# Revit family: Mixer-Sink-Caroma Saracom
name_source: partatom
category: Plumbing Fixtures
revit_build: Autodesk Revit 2014 (Build: 20131024_2115(x64)
units: mm (PartAtom-declared; Revit-internal decimal feet)

## types (1)
- Standard
    Assembly Code = D2020300
    CW Connection = Yes
    CWFU = 1.98
    Connector Radius = 10 mm  [stored 0.0328084 ft]
    Cost = 0 $
    Default Elevation = 0 mm  [stored 0 ft]
    Description = The Saracom range offers the home owner the practical choice in using one stylish mixer design for the entire home, from the kitchen to the laundry to the bathroom.
    HW Connection = Yes
    HWFU = 1.98
    Height_ANZRS = 272 mm
    Length_ANZRS = 123 mm  [stored 0.403543 ft]
    Manufacturer = GWA Bathrooms & Kitchens
    Material_ANZRS = Metal-Chrome-Caroma
    Model = 98025C4A
    ModifiedIssue_ANZRS = 20141201.01 $
    Type Comments = Caroma Saracom Sink Mixer
    URL = http://specify.caroma.com.au
    Vent Connection = No
    WELSRating_ANZRS = WELS 4 Star rated, 7.5L/min
    Waste Connection = No
    Width_ANZRS = 23 mm  [stored 0.0754593 ft]

note: [stored X ft] marks values corroborated as IEEE doubles in the binary element streams (Revit-internal decimal feet)

## geometry (parser evidence)
native form markers: Blend x8, Sweep x1
no freeform markers — native parametric forms only
